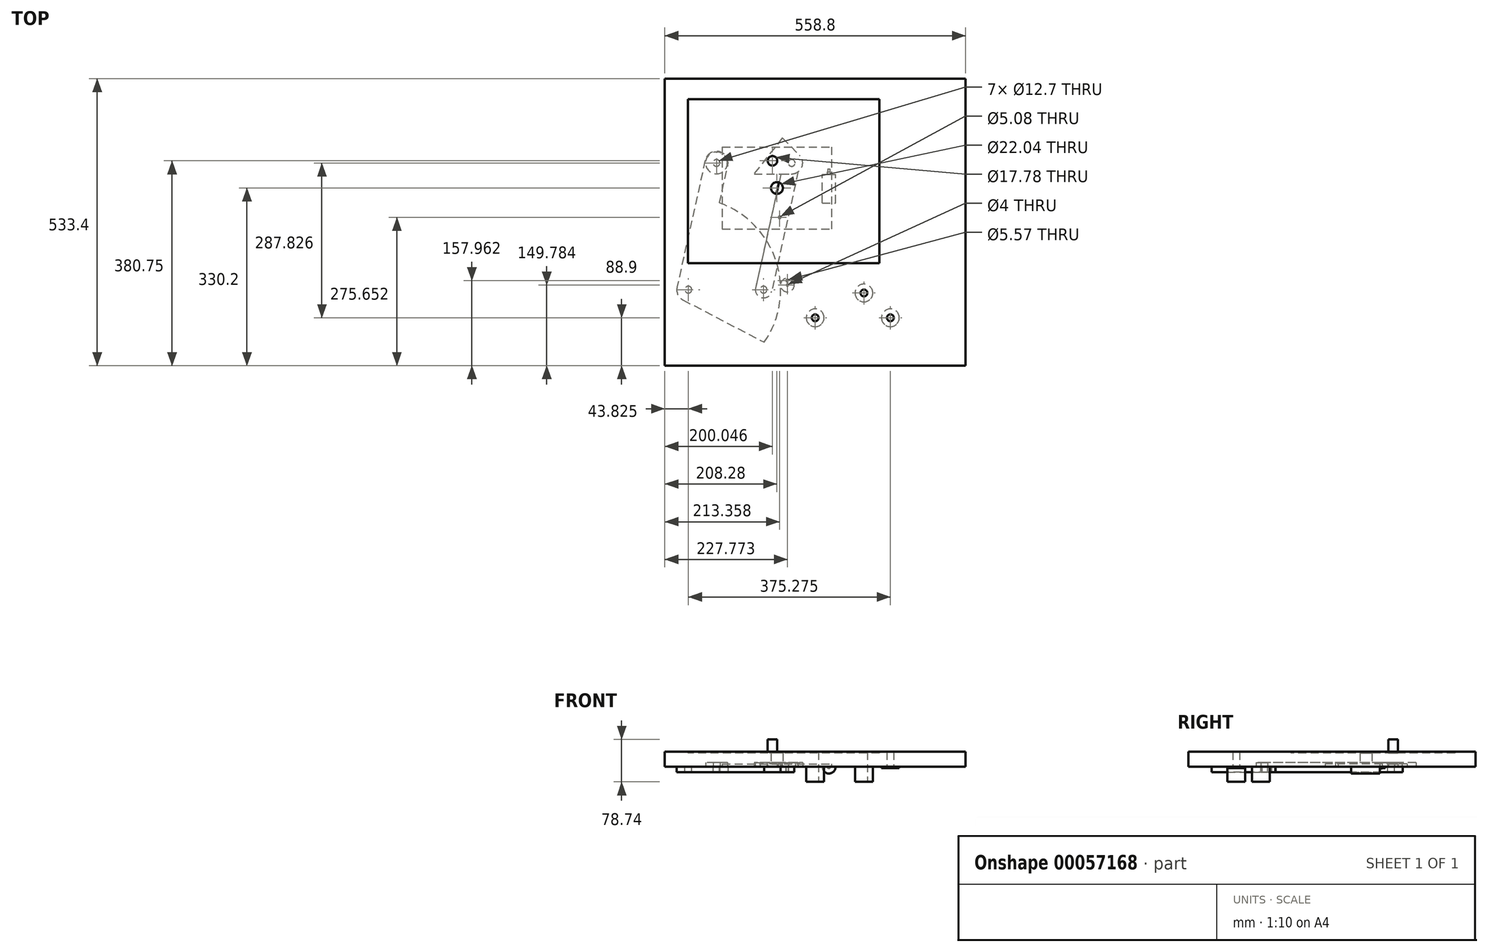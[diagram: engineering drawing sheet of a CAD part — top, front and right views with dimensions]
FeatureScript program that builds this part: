
annotation { "Feature Type Name" : "Feature", "Feature Type Description" : "" }
export const myFeature = defineFeature(function(context is Context, id is Id, definition is map)
    precondition{}
    {
        {
            var Q0;
            Q0=qCreatedBy(makeId("Top.planeOp"),FACE);
            var sketch = newSketch(context, id + "F0", { "sketchPlane" : qUnion([Q0])});
            skLineSegment(sketch, "E0.bottom", {"start": v(-304.8, 177.8) * mm, "end": v(254, 177.8) * mm});
            skLineSegment(sketch, "E0.top", {"start": v(-304.8, -355.6) * mm, "end": v(254, -355.6) * mm});
            skLineSegment(sketch, "E0.left", {"start": v(-304.8, 177.8) * mm, "end": v(-304.8, -355.6) * mm});
            skLineSegment(sketch, "E0.right", {"start": v(254, 177.8) * mm, "end": v(254, -355.6) * mm});
            skLineSegment(sketch, "E1", {"start": v(0, 177.8) * mm, "end": v(0, 0) * mm, "construction": true});
            skPoint(sketch, "E2.rect.middle", {"position": v(0, 0) * mm});
            skPoint(sketch, "E3", {"position": v(0, -266.7) * mm});
            skPoint(sketch, "E4", {"position": v(-25.4, -266.7) * mm});
            skArc(sketch, "E5", {"start": v(-198.12, -98.2) * mm, "mid": v(-257.36, -200.22) * mm, "end": v(-261.15, -318.14) * mm});
            skLineSegment(sketch, "E6", {"start": v(-25.4, -266.7) * mm, "end": v(-260.97, -214.45) * mm});
            skLineSegment(sketch, "E7", {"start": v(-260.97, -214.45) * mm, "end": v(-208.72, 21.13) * mm});
            skLineSegment(sketch, "E8", {"start": v(-69.02, 21.13) * mm, "end": v(-121.27, -214.45) * mm});
            skLineSegment(sketch, "E9", {"start": v(-121.27, -214.45) * mm, "end": v(114.3, -266.7) * mm});
            skPoint(sketch, "E10.rect.middle", {"position": v(-96.52, -25.4) * mm});
            skLineSegment(sketch, "E11.rect.bottom", {"start": v(5.08, 50.8) * mm, "end": v(-198.12, 50.8) * mm});
            skLineSegment(sketch, "E11.rect.top", {"start": v(5.08, -101.6) * mm, "end": v(-198.12, -101.6) * mm});
            skLineSegment(sketch, "E11.rect.left", {"start": v(5.08, 50.8) * mm, "end": v(5.08, -101.6) * mm});
            skLineSegment(sketch, "E11.rect.right", {"start": v(-198.12, 50.8) * mm, "end": v(-198.12, -101.6) * mm});
            skArc(sketch, "E12", {"start": v(-94.35, -39.92) * mm, "mid": v(-206.01, 20.5) * mm, "end": v(-332.89, 15.89) * mm});
            skLineSegment(sketch, "E13", {"start": v(-225.15, -131.33) * mm, "end": v(-263.65, -304.92) * mm});
            skLineSegment(sketch, "E14", {"start": v(-312.77, 21.23) * mm, "end": v(-114.4, -22.77) * mm});
            skLineSegment(sketch, "E15", {"start": v(-208.72, 21.13) * mm, "end": v(-69.02, 21.13) * mm});
            skLineSegment(sketch, "E16", {"start": v(-118.18, 67.22) * mm, "end": v(117.4, 14.97) * mm});
            skLineSegment(sketch, "E17", {"start": v(117.4, 14.97) * mm, "end": v(65.14, -220.6) * mm});
            skLineSegment(sketch, "E18", {"start": v(-118.18, 67.22) * mm, "end": v(-208.72, 21.13) * mm});
            skLineSegment(sketch, "E19", {"start": v(-118.18, 67.22) * mm, "end": v(-69.02, 21.13) * mm});
            skLineSegment(sketch, "E20", {"start": v(-25.4, -266.7) * mm, "end": v(65.14, -220.6) * mm});
            skLineSegment(sketch, "E21", {"start": v(65.14, -220.6) * mm, "end": v(114.3, -266.7) * mm});
            skLineSegment(sketch, "E22", {"start": v(-25.4, -266.7) * mm, "end": v(114.3, -266.7) * mm});
            skArc(sketch, "E23", {"start": v(237.2, -51.44) * mm, "mid": v(120.46, 14.27) * mm, "end": v(-13.34, 7.57) * mm});
            skArc(sketch, "E24", {"start": v(-40.45, 197.48) * mm, "mid": v(-119.83, 59.13) * mm, "end": v(-95.56, -98.5) * mm});
            skLineSegment(sketch, "E25", {"start": v(13.35, 15.07) * mm, "end": v(211.73, -28.93) * mm});
            skLineSegment(sketch, "E26", {"start": v(-82.36, 150.33) * mm, "end": v(-120.86, -23.25) * mm});
            skLineSegment(sketch, "E27.bottom", {"start": v(-261.62, 139.7) * mm, "end": v(93.98, 139.7) * mm});
            skLineSegment(sketch, "E27.top", {"start": v(-261.62, -165.1) * mm, "end": v(93.98, -165.1) * mm});
            skLineSegment(sketch, "E27.left", {"start": v(-261.62, 139.7) * mm, "end": v(-261.62, -165.1) * mm});
            skLineSegment(sketch, "E27.right", {"start": v(93.98, 139.7) * mm, "end": v(93.98, -165.1) * mm});
            skLineSegment(sketch, "E28", {"start": v(-198.12, 50.8) * mm, "end": v(5.08, -101.6) * mm});
            skSolve(sketch);
        }
        {
            var Q0;
            Q0=qCreatedBy(makeId("Top.planeOp"),FACE);
            var sketch = newSketch(context, id + "F1", { "sketchPlane" : qUnion([Q0])});
            skLineSegment(sketch, "E29", {"start": v(114.3, -266.7) * mm, "end": v(230.76, -266.7) * mm});
            skLineSegment(sketch, "E30", {"start": v(-121.27, -214.45) * mm, "end": v(-69.02, 21.13) * mm, "construction": true});
            skLineSegment(sketch, "E31", {"start": v(114.3, -266.7) * mm, "end": v(-121.27, -214.45) * mm, "construction": true});
            skLineSegment(sketch, "E32", {"start": v(0, 0) * mm, "end": v(0, -120.25) * mm});
            skLineSegment(sketch, "E33.bottom", {"start": v(-261.62, -165.1) * mm, "end": v(93.98, -165.1) * mm, "construction": true});
            skLineSegment(sketch, "E33.top", {"start": v(-261.62, 139.7) * mm, "end": v(93.98, 139.7) * mm, "construction": true});
            skLineSegment(sketch, "E33.left", {"start": v(-261.62, -165.1) * mm, "end": v(-261.62, 139.7) * mm, "construction": true});
            skLineSegment(sketch, "E33.right", {"start": v(93.98, -165.1) * mm, "end": v(93.98, 139.7) * mm, "construction": true});
            skLineSegment(sketch, "E34", {"start": v(-25.4, -266.7) * mm, "end": v(-260.97, -214.45) * mm, "construction": true});
            skLineSegment(sketch, "E35", {"start": v(-260.97, -214.45) * mm, "end": v(-208.72, 21.13) * mm, "construction": true});
            skLineSegment(sketch, "E36", {"start": v(-208.72, 21.13) * mm, "end": v(-69.02, 21.13) * mm, "construction": true});
            skLineSegment(sketch, "E37", {"start": v(-25.4, -266.7) * mm, "end": v(114.3, -266.7) * mm, "construction": true});
            skLineSegment(sketch, "E38.bottom", {"start": v(-304.8, 177.8) * mm, "end": v(254, 177.8) * mm});
            skLineSegment(sketch, "E38.top", {"start": v(-304.8, -355.6) * mm, "end": v(254, -355.6) * mm});
            skLineSegment(sketch, "E38.left", {"start": v(-304.8, 177.8) * mm, "end": v(-304.8, -355.6) * mm});
            skLineSegment(sketch, "E38.right", {"start": v(254, 177.8) * mm, "end": v(254, -355.6) * mm});
            skPoint(sketch, "E39.rect.middle", {"position": v(-230.12, 30.7) * mm});
            skLineSegment(sketch, "E40.rect.bottom", {"start": v(5.08, 50.8) * mm, "end": v(-198.12, 50.8) * mm, "construction": true});
            skLineSegment(sketch, "E40.rect.top", {"start": v(5.08, -101.6) * mm, "end": v(-198.12, -101.6) * mm, "construction": true});
            skLineSegment(sketch, "E40.rect.left", {"start": v(5.08, 50.8) * mm, "end": v(5.08, -101.6) * mm, "construction": true});
            skLineSegment(sketch, "E40.rect.right", {"start": v(-198.12, 50.8) * mm, "end": v(-198.12, -101.6) * mm, "construction": true});
            skPoint(sketch, "E40.rect.middle", {"position": v(-96.52, -25.4) * mm});
            skCircle(sketch, "E41", {"center": v(-25.4, -266.7) * mm, "radius": 16.51 * mm, "construction": true});
            skCircle(sketch, "E42", {"center": v(114.3, -266.7) * mm, "radius": 16.51 * mm, "construction": true});
            skLineSegment(sketch, "E43", {"start": v(-69.02, 21.13) * mm, "end": v(114.3, -266.7) * mm, "construction": true});
            skLineSegment(sketch, "E44", {"start": v(-118.18, 67.22) * mm, "end": v(117.4, 14.97) * mm, "construction": true});
            skCircle(sketch, "E45", {"center": v(-25.4, -266.7) * mm, "radius": 6.35 * mm});
            skCircle(sketch, "E46", {"center": v(114.3, -266.7) * mm, "radius": 6.35 * mm});
            skCircle(sketch, "E47", {"center": v(65.14, -220.6) * mm, "radius": 6.35 * mm});
            skLineSegment(sketch, "E48", {"start": v(117.4, 14.97) * mm, "end": v(65.14, -220.6) * mm, "construction": true});
            skCircle(sketch, "E49", {"center": v(-96.52, -25.4) * mm, "radius": 11.02 * mm});
            skCircle(sketch, "E50", {"center": v(65.14, -220.6) * mm, "radius": 16.51 * mm, "construction": true});
            skSolve(sketch);
        }
        {
            var Q0;
            Q0=qCreatedBy(makeId("Top.planeOp"),FACE);
            var sketch = newSketch(context, id + "F2", { "sketchPlane" : qUnion([Q0])});
            skCircle(sketch, "E51", {"center": v(-260.97, -214.45) * mm, "radius": 21.6 * mm});
            skCircle(sketch, "E52", {"center": v(-208.72, 21.13) * mm, "radius": 21.59 * mm});
            skArc(sketch, "E53", {"start": v(-120.09, -312.15) * mm, "mid": v(-105.58, -142) * mm, "end": v(-245.22, -43.72) * mm});
            skCircle(sketch, "E54", {"center": v(-77.03, -205.82) * mm, "radius": 12.7 * mm});
            skLineSegment(sketch, "E55", {"start": v(-239.9, -219.12) * mm, "end": v(-187.65, 16.45) * mm});
            skLineSegment(sketch, "E56", {"start": v(-229.8, 25.8) * mm, "end": v(-282.05, -209.77) * mm});
            skLineSegment(sketch, "E57", {"start": v(-270.95, -233.6) * mm, "end": v(-120.09, -312.15) * mm});
            skCircle(sketch, "E58", {"center": v(-260.97, -214.45) * mm, "radius": 6.35 * mm});
            skCircle(sketch, "E59", {"center": v(-208.72, 21.13) * mm, "radius": 6.35 * mm});
            skCircle(sketch, "E60", {"center": v(-77.03, -205.82) * mm, "radius": 2 * mm});
            skCircle(sketch, "E61", {"center": v(-77.03, -197.64) * mm, "radius": 2.79 * mm});
            skLineSegment(sketch, "E62", {"start": v(-77.03, -205.82) * mm, "end": v(-77.03, -197.64) * mm});
            skLineSegment(sketch, "E63", {"start": v(-260.97, -214.45) * mm, "end": v(-108.9, -293.63) * mm, "construction": true});
            skLineSegment(sketch, "E64", {"start": v(-77.03, -205.82) * mm, "end": v(-260.97, -214.45) * mm, "construction": true});
            skSolve(sketch);
        }
        {
            var Q0;
            Q0=qCreatedBy(makeId("Top.planeOp"),FACE);
            var sketch = newSketch(context, id + "F3", { "sketchPlane" : qUnion([Q0])});
            skCircle(sketch, "E65", {"center": v(-121.27, -214.45) * mm, "radius": 15.24 * mm});
            skCircle(sketch, "E66", {"center": v(-69.02, 21.13) * mm, "radius": 15.24 * mm});
            skLineSegment(sketch, "E67", {"start": v(-83.9, 24.43) * mm, "end": v(-136.15, -211.15) * mm});
            skLineSegment(sketch, "E68", {"start": v(-54.15, 17.83) * mm, "end": v(-106.4, -217.75) * mm});
            skCircle(sketch, "E69", {"center": v(-69.02, 21.13) * mm, "radius": 6.35 * mm});
            skCircle(sketch, "E70", {"center": v(-121.27, -214.45) * mm, "radius": 6.35 * mm});
            skCircle(sketch, "E71", {"center": v(-91.44, -79.95) * mm, "radius": 2.54 * mm});
            skSolve(sketch);
        }
        {
            var Q0;
            Q0=makeQuery(id+"F3.imprint","IMPRINT",FACE,{"disambiguationData":[TD([[makeQuery(id+"F3.imprint","IMPRINT",EDGE,{"derivedFrom":sQuery(id+"F3.wireOp",EDGE,"E69")}),-1.0]])]});
            var Q1;
            {var subQ1=sQuery(id+"F3.wireOp",EDGE,"E67");Q1=makeQuery(id+"F3.imprint","IMPRINT",FACE,{"disambiguationData":[TD([[makeQuery(id+"F3.imprint","IMPRINT",EDGE,{"derivedFrom":subQ1}),1.0]])]});}
            var Q2;
            Q2=makeQuery(id+"F3.imprint","IMPRINT",FACE,{"disambiguationData":[TD([[makeQuery(id+"F3.imprint","IMPRINT",EDGE,{"derivedFrom":sQuery(id+"F3.wireOp",EDGE,"E70")}),-1.0]])]});
            extrude(context, id + "F4", {"entities" : qUnion([Q0, Q1, Q2]), "depth" : 7.62 * mm});
        }
        {
            var Q0;
            Q0=makeQuery(id+"F2.imprint","IMPRINT",FACE,{"disambiguationData":[TD([[makeQuery(id+"F2.imprint","IMPRINT",EDGE,{"derivedFrom":sQuery(id+"F2.wireOp",EDGE,"E59")}),-1.0]])]});
            var Q1;
            {var subQ1=sQuery(id+"F2.wireOp",EDGE,"E52");var subQ5=sQuery(id+"F2.wireOp",EDGE,"E55");var subQ7=makeQuery(id+"F2.imprint","INTERSECT",VERTEX,{"derivedFrom":[subQ1,subQ5]});Q1=makeQuery(id+"F2.imprint","IMPRINT",FACE,{"disambiguationData":[TD([[makeQuery(id+"F2.imprint","IMPRINT",EDGE,{"disambiguationData":[TD([[subQ7,1.0]])],"derivedFrom":subQ1}),-1.0]])]});}
            var Q2;
            {var subQ0=sQuery(id+"F2.wireOp",EDGE,"E55");var subQ3=sQuery(id+"F2.wireOp",EDGE,"E51");var subQ4=makeQuery(id+"F2.imprint","INTERSECT",VERTEX,{"derivedFrom":[subQ3,subQ0]});Q2=makeQuery(id+"F2.imprint","IMPRINT",FACE,{"disambiguationData":[TD([[makeQuery(id+"F2.imprint","IMPRINT",EDGE,{"disambiguationData":[TD([[subQ4,-1.0]])],"derivedFrom":subQ3}),-1.0]])]});}
            var Q3;
            Q3=makeQuery(id+"F2.imprint","IMPRINT",FACE,{"disambiguationData":[TD([[makeQuery(id+"F2.imprint","IMPRINT",EDGE,{"derivedFrom":sQuery(id+"F2.wireOp",EDGE,"E58")}),-1.0]])]});
            var Q4;
            {var subQ0=sQuery(id+"F2.wireOp",EDGE,"E57");Q4=makeQuery(id+"F2.imprint","IMPRINT",FACE,{"disambiguationData":[TD([[makeQuery(id+"F2.imprint","IMPRINT",EDGE,{"derivedFrom":subQ0}),1.0]])]});}
            extrude(context, id + "F5", {"entities" : qUnion([Q0, Q1, Q2, Q3, Q4]), "oppositeDirection" : true, "depth" : 10.16 * mm});
        }
        {
            var Q0;
            Q0=makeQuery(id+"F2.imprint","IMPRINT",FACE,{"disambiguationData":[TD([[makeQuery(id+"F2.imprint","IMPRINT",EDGE,{"derivedFrom":sQuery(id+"F2.wireOp",EDGE,"E54")}),1.0]])]});
            extrude(context, id + "F6", {"entities" : qUnion([Q0]), "oppositeDirection" : true, "depth" : 10.16 * mm});
        }
        {
            var Q0;
            {var subQ5=sQuery(id+"F1.wireOp",EDGE,"E38.bottom");Q0=makeQuery(id+"F1.imprint","IMPRINT",FACE,{"disambiguationData":[TD([[makeQuery(id+"F1.imprint","IMPRINT",EDGE,{"derivedFrom":subQ5}),-1.0]])]});}
            extrude(context, id + "F7", {"entities" : qUnion([Q0]), "depth" : 25.4 * mm});
        }
        {
            var Q0;
            Q0=qCreatedBy(makeId("Top.planeOp"),FACE);
            var sketch = newSketch(context, id + "F8", { "sketchPlane" : qUnion([Q0])});
            skCircle(sketch, "E72", {"center": v(-77.03, -205.82) * mm, "radius": 37.41 * mm});
            skCircle(sketch, "E73", {"center": v(-260.97, -214.45) * mm, "radius": 23.1 * mm});
            skCircle(sketch, "E74", {"center": v(-25.4, -266.7) * mm, "radius": 20.32 * mm});
            skLineSegment(sketch, "E75", {"start": v(-7.45, -257.18) * mm, "end": v(-43.97, -188.3) * mm});
            skLineSegment(sketch, "E76", {"start": v(-81.68, -168.7) * mm, "end": v(-263.85, -191.52) * mm});
            skLineSegment(sketch, "E77", {"start": v(-29.57, -286.59) * mm, "end": v(-265.72, -237.06) * mm});
            skCircle(sketch, "E78", {"center": v(-260.97, -214.45) * mm, "radius": 6.35 * mm});
            skCircle(sketch, "E79", {"center": v(-72.41, -214.89) * mm, "radius": 9.53 * mm});
            skCircle(sketch, "E80", {"center": v(-25.4, -266.7) * mm, "radius": 6.35 * mm});
            skSolve(sketch);
        }
        {
            var Q0;
            {var subQ1=sQuery(id+"F8.wireOp",EDGE,"E75");Q0=makeQuery(id+"F8.imprint","IMPRINT",FACE,{"disambiguationData":[TD([[makeQuery(id+"F8.imprint","IMPRINT",EDGE,{"derivedFrom":subQ1}),1.0]])]});}
            var Q1;
            Q1=makeQuery(id+"F8.imprint","IMPRINT",FACE,{"disambiguationData":[TD([[makeQuery(id+"F8.imprint","IMPRINT",EDGE,{"derivedFrom":sQuery(id+"F8.wireOp",EDGE,"E80")}),-1.0]])]});
            var Q2;
            Q2=makeQuery(id+"F8.imprint","IMPRINT",FACE,{"disambiguationData":[TD([[makeQuery(id+"F8.imprint","IMPRINT",EDGE,{"derivedFrom":sQuery(id+"F8.wireOp",EDGE,"E79")}),-1.0]])]});
            var Q3;
            {var subQ0=sQuery(id+"F8.wireOp",EDGE,"E76");Q3=makeQuery(id+"F8.imprint","IMPRINT",FACE,{"disambiguationData":[TD([[makeQuery(id+"F8.imprint","IMPRINT",EDGE,{"derivedFrom":subQ0}),1.0]])]});}
            var Q4;
            Q4=makeQuery(id+"F8.imprint","IMPRINT",FACE,{"disambiguationData":[TD([[makeQuery(id+"F8.imprint","IMPRINT",EDGE,{"derivedFrom":sQuery(id+"F8.wireOp",EDGE,"E78")}),-1.0]])]});
            var Q5;
            {var subQ0=sQuery(id+"F8.wireOp",EDGE,"E73");var subQ1=sQuery(id+"F8.wireOp",EDGE,"E72");var subQ3=makeQuery(id+"F8.imprint","INTERSECT",VERTEX,{"disambiguationData":[OD(0.0)],"derivedFrom":[subQ1,subQ0]});Q5=makeQuery(id+"F8.imprint","IMPRINT",FACE,{"disambiguationData":[TD([[makeQuery(id+"F8.imprint","IMPRINT",EDGE,{"disambiguationData":[TD([[subQ3,1.0]])],"derivedFrom":subQ1}),1.0]])]});}
            extrude(context, id + "F9", {"entities" : qUnion([Q0, Q1, Q2, Q3, Q4, Q5]), "depth" : 7.62 * mm});
        }
        {
            var Q0;
            Q0=qCreatedBy(makeId("Top.planeOp"),FACE);
            var sketch = newSketch(context, id + "F10", { "sketchPlane" : qUnion([Q0])});
            skCircle(sketch, "E81", {"center": v(-208.72, 21.13) * mm, "radius": 20.32 * mm});
            skCircle(sketch, "E82", {"center": v(-69.02, 21.13) * mm, "radius": 20.32 * mm});
            skLineSegment(sketch, "E83", {"start": v(-208.72, 0.8) * mm, "end": v(-69.02, 0.8) * mm});
            skLineSegment(sketch, "E84", {"start": v(-187.07, 41.45) * mm, "end": v(-69.02, 41.45) * mm});
            skCircle(sketch, "E85", {"center": v(-69.02, 21.13) * mm, "radius": 6.35 * mm});
            skCircle(sketch, "E86", {"center": v(-208.72, 21.13) * mm, "radius": 6.35 * mm});
            skSolve(sketch);
        }
        {
            var Q0;
            {var subQ0=sQuery(id+"F10.wireOp",EDGE,"E83");Q0=makeQuery(id+"F10.imprint","IMPRINT",FACE,{"disambiguationData":[TD([[makeQuery(id+"F10.imprint","IMPRINT",EDGE,{"derivedFrom":subQ0}),1.0]])]});}
            var Q1;
            Q1=makeQuery(id+"F10.imprint","IMPRINT",FACE,{"disambiguationData":[TD([[makeQuery(id+"F10.imprint","IMPRINT",EDGE,{"derivedFrom":sQuery(id+"F10.wireOp",EDGE,"E85")}),-1.0]])]});
            var Q2;
            Q2=makeQuery(id+"F10.imprint","IMPRINT",FACE,{"disambiguationData":[TD([[makeQuery(id+"F10.imprint","IMPRINT",EDGE,{"derivedFrom":sQuery(id+"F10.wireOp",EDGE,"E86")}),-1.0]])]});
            extrude(context, id + "F11", {"entities" : qUnion([Q0, Q1, Q2]), "depth" : 7.62 * mm});
        }
        {
            var Q0;
            Q0=qCreatedBy(makeId("Top.planeOp"),FACE);
            var sketch = newSketch(context, id + "F12", { "sketchPlane" : qUnion([Q0])});
            skCircle(sketch, "E87", {"center": v(-208.72, 21.13) * mm, "radius": 6.35 * mm});
            skCircle(sketch, "E88", {"center": v(-69.02, 21.13) * mm, "radius": 6.35 * mm});
            skCircle(sketch, "E89", {"center": v(-118.18, 67.22) * mm, "radius": 6.35 * mm});
            skCircle(sketch, "E90", {"center": v(-208.72, 21.13) * mm, "radius": 20.32 * mm});
            skCircle(sketch, "E91", {"center": v(-118.18, 67.22) * mm, "radius": 22.86 * mm});
            skCircle(sketch, "E92", {"center": v(-69.02, 21.13) * mm, "radius": 20.32 * mm});
            skLineSegment(sketch, "E93", {"start": v(-208.72, 0.8) * mm, "end": v(-69.02, 0.8) * mm});
            skLineSegment(sketch, "E94", {"start": v(-218.4, 39) * mm, "end": v(-129.06, 87.32) * mm});
            skLineSegment(sketch, "E95", {"start": v(-101.93, 83.3) * mm, "end": v(-54.58, 35.41) * mm});
            skLineSegment(sketch, "E96", {"start": v(-86.42, 67.6) * mm, "end": v(-138.87, 0.8) * mm});
            skSolve(sketch);
        }
        {
            var Q0;
            Q0=makeQuery(id+"F12.imprint","IMPRINT",FACE,{"disambiguationData":[TD([[makeQuery(id+"F12.imprint","IMPRINT",EDGE,{"derivedFrom":sQuery(id+"F12.wireOp",EDGE,"E88")}),-1.0]])]});
            var Q1;
            {var subQ2=sQuery(id+"F12.wireOp",EDGE,"E93");Q1=makeQuery(id+"F12.imprint","IMPRINT",FACE,{"disambiguationData":[TD([[makeQuery(id+"F12.imprint","IMPRINT",EDGE,{"derivedFrom":subQ2}),1.0]])]});}
            var Q2;
            Q2=makeQuery(id+"F12.imprint","IMPRINT",FACE,{"disambiguationData":[TD([[makeQuery(id+"F12.imprint","IMPRINT",EDGE,{"derivedFrom":sQuery(id+"F12.wireOp",EDGE,"E89")}),-1.0]])]});
            var Q3;
            Q3=makeQuery(id+"F12.imprint","IMPRINT",FACE,{"disambiguationData":[TD([[makeQuery(id+"F12.imprint","IMPRINT",EDGE,{"derivedFrom":sQuery(id+"F12.wireOp",EDGE,"E87")}),-1.0]])]});
            var Q4;
            {var subQ4=sQuery(id+"F12.wireOp",EDGE,"E94");Q4=makeQuery(id+"F12.imprint","IMPRINT",FACE,{"disambiguationData":[TD([[makeQuery(id+"F12.imprint","IMPRINT",EDGE,{"derivedFrom":subQ4}),-1.0]])]});}
            extrude(context, id + "F13", {"entities" : qUnion([Q0, Q1, Q2, Q3, Q4]), "depth" : 22.86 * mm});
        }
        {
            var Q0;
            Q0=qCreatedBy(makeId("Front.planeOp"),FACE);
            var sketch = newSketch(context, id + "F14", { "sketchPlane" : qUnion([Q0])});
            skCircle(sketch, "E97", {"center": v(0, 0) * mm, "radius": 12.5 * mm});
            skCircle(sketch, "E98", {"center": v(0, 0) * mm, "radius": 3.18 * mm});
            skCircle(sketch, "E99", {"center": v(0, 0) * mm, "radius": 2 * mm});
            skSolve(sketch);
        }
        {
            var Q0;
            Q0=makeQuery(id+"F14.imprint","IMPRINT",FACE,{"disambiguationData":[TD([[makeQuery(id+"F14.imprint","IMPRINT",EDGE,{"derivedFrom":sQuery(id+"F14.wireOp",EDGE,"E97")}),1.0]])]});
            var Q1;
            Q1=makeQuery(id+"F14.imprint","IMPRINT",FACE,{"disambiguationData":[TD([[makeQuery(id+"F14.imprint","IMPRINT",EDGE,{"derivedFrom":sQuery(id+"F14.wireOp",EDGE,"E98")}),1.0]])]});
            var Q2;
            Q2=makeQuery(id+"F14.imprint","IMPRINT",FACE,{"disambiguationData":[TD([[makeQuery(id+"F14.imprint","IMPRINT",EDGE,{"derivedFrom":sQuery(id+"F14.wireOp",EDGE,"E99")}),1.0]])]});
            extrude(context, id + "F15", {"entities" : qUnion([Q0, Q1, Q2]), "depth" : 53.34 * mm});
        }
        {
            var Q0;
            Q0=makeQuery(id+"F14.imprint","IMPRINT",FACE,{"disambiguationData":[TD([[makeQuery(id+"F14.imprint","IMPRINT",EDGE,{"derivedFrom":sQuery(id+"F14.wireOp",EDGE,"E98")}),1.0]])]});
            var Q1;
            Q1=makeQuery(id+"F14.imprint","IMPRINT",FACE,{"disambiguationData":[TD([[makeQuery(id+"F14.imprint","IMPRINT",EDGE,{"derivedFrom":sQuery(id+"F14.wireOp",EDGE,"E99")}),1.0]])]});
            extrude(context, id + "F16", {"entities" : qUnion([Q0, Q1]), "operationType" : NewBodyOperationType.ADD, "oppositeDirection" : true, "depth" : 4.57 * mm});
        }
        {
            var Q0;
            Q0=makeQuery(id+"F14.imprint","IMPRINT",FACE,{"disambiguationData":[TD([[makeQuery(id+"F14.imprint","IMPRINT",EDGE,{"derivedFrom":sQuery(id+"F14.wireOp",EDGE,"E99")}),1.0]])]});
            extrude(context, id + "F17", {"entities" : qUnion([Q0]), "operationType" : NewBodyOperationType.ADD, "oppositeDirection" : true, "depth" : 10.16 * mm});
        }
        {
            var Q0;
            Q0=makeQuery(id+"F7.opExtrude","CAP_FACE",FACE,{"disambiguationData":[OSD([sQuery(id+"F1.wireOp",EDGE,"E38.bottom"),sQuery(id+"F1.wireOp",EDGE,"E38.top"),sQuery(id+"F1.wireOp",EDGE,"E38.left"),sQuery(id+"F1.wireOp",EDGE,"E38.right"),sQuery(id+"F1.wireOp",EDGE,"E45"),sQuery(id+"F1.wireOp",EDGE,"E46"),sQuery(id+"F1.wireOp",EDGE,"E47")])],"isStart":false});
            var sketch = newSketch(context, id + "F18", { "sketchPlane" : qUnion([Q0])});
            skLineSegment(sketch, "E100.bottom", {"start": v(93.98, 139.7) * mm, "end": v(-261.62, 139.7) * mm});
            skLineSegment(sketch, "E100.top", {"start": v(93.98, -165.1) * mm, "end": v(-261.62, -165.1) * mm});
            skLineSegment(sketch, "E100.left", {"start": v(93.98, 139.7) * mm, "end": v(93.98, -165.1) * mm});
            skLineSegment(sketch, "E100.right", {"start": v(-261.62, 139.7) * mm, "end": v(-261.62, -165.1) * mm});
            skSolve(sketch);
        }
        {
            var Q0;
            Q0=makeQuery(id+"F18.imprint","IMPRINT",FACE,{"disambiguationData":[TD([[makeQuery(id+"F18.imprint","IMPRINT",EDGE,{"derivedFrom":sQuery(id+"F18.wireOp",EDGE,"E100.bottom")}),-1.0]])]});
            extrude(context, id + "F19", {"entities" : qUnion([Q0]), "operationType" : NewBodyOperationType.ADD, "depth" : 2.54 * mm});
        }
        {
            var Q0;
            Q0=qCreatedBy(makeId("Top.planeOp"),FACE);
            var sketch = newSketch(context, id + "F20", { "sketchPlane" : qUnion([Q0])});
            skCircle(sketch, "E101", {"center": v(-121.27, -214.45) * mm, "radius": 14.89 * mm});
            skCircle(sketch, "E102", {"center": v(114.3, -266.7) * mm, "radius": 15.82 * mm});
            skLineSegment(sketch, "E103", {"start": v(-118.1, -199.9) * mm, "end": v(117.67, -251.24) * mm});
            skLineSegment(sketch, "E104", {"start": v(-124.55, -228.97) * mm, "end": v(110.81, -282.13) * mm});
            skCircle(sketch, "E105", {"center": v(-121.27, -214.45) * mm, "radius": 7.18 * mm});
            skCircle(sketch, "E106", {"center": v(114.3, -266.7) * mm, "radius": 7.53 * mm});
            skSolve(sketch);
        }
        {
            var Q0;
            Q0=makeQuery(id+"F20.imprint","IMPRINT",FACE,{"disambiguationData":[TD([[makeQuery(id+"F20.imprint","IMPRINT",EDGE,{"derivedFrom":sQuery(id+"F20.wireOp",EDGE,"E105")}),-1.0]])]});
            var Q1;
            {var subQ1=sQuery(id+"F20.wireOp",EDGE,"E103");Q1=makeQuery(id+"F20.imprint","IMPRINT",FACE,{"disambiguationData":[TD([[makeQuery(id+"F20.imprint","IMPRINT",EDGE,{"derivedFrom":subQ1}),-1.0]])]});}
            var Q2;
            Q2=makeQuery(id+"F20.imprint","IMPRINT",FACE,{"disambiguationData":[TD([[makeQuery(id+"F20.imprint","IMPRINT",EDGE,{"derivedFrom":sQuery(id+"F20.wireOp",EDGE,"E106")}),-1.0]])]});
            extrude(context, id + "F21", {"entities" : qUnion([Q0, Q1, Q2]), "depth" : 7.62 * mm});
        }
        {
            var Q0;
            Q0=makeQuery(id+"F7.opExtrude","CAP_FACE",FACE,{"disambiguationData":[OSD([sQuery(id+"F1.wireOp",EDGE,"E38.bottom"),sQuery(id+"F1.wireOp",EDGE,"E38.top"),sQuery(id+"F1.wireOp",EDGE,"E38.left"),sQuery(id+"F1.wireOp",EDGE,"E38.right"),sQuery(id+"F1.wireOp",EDGE,"E45"),sQuery(id+"F1.wireOp",EDGE,"E46"),sQuery(id+"F1.wireOp",EDGE,"E47"),sQuery(id+"F1.wireOp",EDGE,"E49")])],"isStart":true});
            var sketch = newSketch(context, id + "F22", { "sketchPlane" : qUnion([Q0])});
            skCircle(sketch, "E107", {"center": v(-25.4, 266.7) * mm, "radius": 16.51 * mm});
            skCircle(sketch, "E108", {"center": v(65.14, 220.6) * mm, "radius": 16.51 * mm});
            skCircle(sketch, "E109", {"center": v(114.3, 266.7) * mm, "radius": 16.51 * mm});
            skSolve(sketch);
        }
        {
            var Q0;
            Q0=makeQuery(id+"F22.imprint","IMPRINT",FACE,{"disambiguationData":[TD([[makeQuery(id+"F22.imprint","IMPRINT",EDGE,{"derivedFrom":sQuery(id+"F22.wireOp",EDGE,"E107")}),1.0]])]});
            var Q1;
            Q1=makeQuery(id+"F22.imprint","IMPRINT",FACE,{"disambiguationData":[TD([[makeQuery(id+"F22.imprint","IMPRINT",EDGE,{"derivedFrom":sQuery(id+"F22.wireOp",EDGE,"E108")}),1.0]])]});
            extrude(context, id + "F23", {"entities" : qUnion([Q0, Q1]), "operationType" : NewBodyOperationType.ADD, "depth" : 27.94 * mm});
        }
        {
            var Q0;
            Q0=makeQuery(id+"F22.imprint","IMPRINT",FACE,{"disambiguationData":[TD([[makeQuery(id+"F22.imprint","IMPRINT",EDGE,{"derivedFrom":sQuery(id+"F22.wireOp",EDGE,"E109")}),1.0]])]});
            extrude(context, id + "F24", {"entities" : qUnion([Q0]), "operationType" : NewBodyOperationType.ADD, "depth" : 2.54 * mm});
        }
        {
            var Q0;
            {var subQ2=sQuery(id+"F12.wireOp",EDGE,"E93");Q0=makeQuery(id+"F12.imprint","IMPRINT",FACE,{"disambiguationData":[TD([[makeQuery(id+"F12.imprint","IMPRINT",EDGE,{"derivedFrom":subQ2}),1.0]])]});}
            var sketch = newSketch(context, id + "F25", { "sketchPlane" : qUnion([Q0])});
            skCircle(sketch, "E110", {"center": v(-104.75, 25.15) * mm, "radius": 8.9 * mm});
            skSolve(sketch);
        }
        {
            var Q0;
            Q0=qSketchRegion(id+"F25",true);
            extrude(context, id + "F26", {"entities" : qUnion([Q0]), "operationType" : NewBodyOperationType.ADD, "depth" : 50.8 * mm});
        }
        {
            var Q0;
            {var subQ0=sQuery(id+"F12.wireOp",EDGE,"E96");Q0=makeQuery(id+"F12.imprint","IMPRINT",FACE,{"disambiguationData":[TD([[makeQuery(id+"F12.imprint","IMPRINT",EDGE,{"derivedFrom":subQ0}),1.0]])]});}
            var Q1;
            Q1=makeQuery(id+"F12.imprint","IMPRINT",FACE,{"disambiguationData":[TD([[makeQuery(id+"F12.imprint","IMPRINT",EDGE,{"derivedFrom":sQuery(id+"F12.wireOp",EDGE,"E88")}),-1.0]])]});
            extrude(context, id + "F27", {"entities" : qUnion([Q0, Q1]), "operationType" : NewBodyOperationType.REMOVE, "depth" : 7.62 * mm});
        }
        {
            var Q0;
            Q0=qCreatedBy(makeId("Top.planeOp"),FACE);
            var sketch = newSketch(context, id + "F28", { "sketchPlane" : qUnion([Q0])});
            skLineSegment(sketch, "E111.bottom", {"start": v(-198.12, 50.8) * mm, "end": v(5.08, 50.8) * mm});
            skLineSegment(sketch, "E111.top", {"start": v(-198.12, -101.6) * mm, "end": v(5.08, -101.6) * mm});
            skLineSegment(sketch, "E111.left", {"start": v(-198.12, 50.8) * mm, "end": v(-198.12, -101.6) * mm});
            skLineSegment(sketch, "E111.right", {"start": v(5.08, 50.8) * mm, "end": v(5.08, -101.6) * mm});
            skCircle(sketch, "E112", {"center": v(-104.75, 25.15) * mm, "radius": 8.9 * mm});
            skSolve(sketch);
        }
        {
            var Q0;
            Q0=makeQuery(id+"F28.imprint","IMPRINT",FACE,{"disambiguationData":[TD([[makeQuery(id+"F28.imprint","IMPRINT",EDGE,{"derivedFrom":sQuery(id+"F28.wireOp",EDGE,"E111.bottom")}),-1.0]])]});
            extrude(context, id + "F29", {"entities" : qUnion([Q0]), "depth" : 5.08 * mm});
        }
    });
